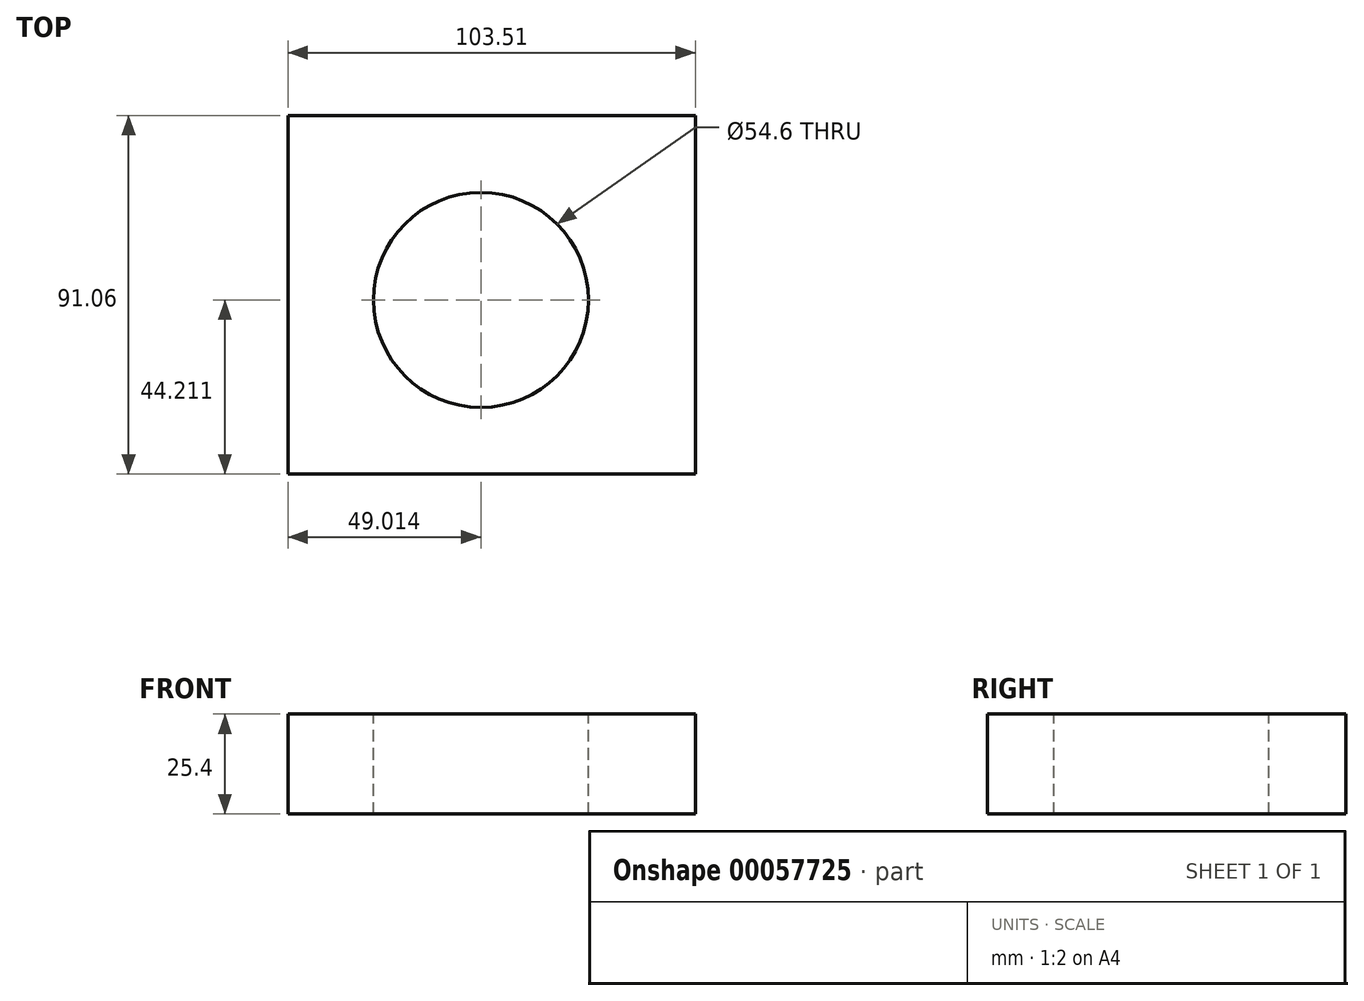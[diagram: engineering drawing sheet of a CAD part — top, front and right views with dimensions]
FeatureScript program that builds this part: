
annotation { "Feature Type Name" : "Feature", "Feature Type Description" : "" }
export const myFeature = defineFeature(function(context is Context, id is Id, definition is map)
    precondition{}
    {
        {
            var Q0;
            Q0=qCreatedBy(makeId("Top.planeOp"),FACE);
            var sketch = newSketch(context, id + "F0", { "sketchPlane" : qUnion([Q0])});
            skLineSegment(sketch, "E0.bottom", {"start": v(-56.32, -38.7) * mm, "end": v(47.2, -38.7) * mm});
            skLineSegment(sketch, "E0.top", {"start": v(-56.32, 52.37) * mm, "end": v(47.2, 52.37) * mm});
            skLineSegment(sketch, "E0.left", {"start": v(-56.32, -38.7) * mm, "end": v(-56.32, 52.37) * mm});
            skLineSegment(sketch, "E0.right", {"start": v(47.2, -38.7) * mm, "end": v(47.2, 52.37) * mm});
            skSolve(sketch);
        }
        {
            var Q0;
            Q0 = qSketchRegion(id + "F0", true);
            extrude(context, id + "F1", {"entities" : qUnion([Q0]), "depth" : 25.4 * mm});
        }
        {
            var Q0;
            Q0=makeQuery(id+"F1.opExtrude","CAP_FACE",FACE,{"disambiguationData":[OSD([sQuery(id+"F0.wireOp",EDGE,"E0.bottom"),sQuery(id+"F0.wireOp",EDGE,"E0.top"),sQuery(id+"F0.wireOp",EDGE,"E0.left"),sQuery(id+"F0.wireOp",EDGE,"E0.right")])],"isStart":false});
            var sketch = newSketch(context, id + "F2", { "sketchPlane" : qUnion([Q0])});
            skCircle(sketch, "E1", {"center": v(-7.3, 5.52) * mm, "radius": 27.3 * mm});
            skSolve(sketch);
        }
        {
            var Q0;
            Q0=makeQuery(id+"F2.imprint","IMPRINT",FACE,{"disambiguationData":[TD([[makeQuery(id+"F2.imprint","IMPRINT",EDGE,{"derivedFrom":sQuery(id+"F2.wireOp",EDGE,"E1")}),1.0]])]});
            extrude(context, id + "F3", {"entities" : qUnion([Q0]), "operationType" : NewBodyOperationType.REMOVE, "endBound" : BoundingType.THROUGH_ALL, "oppositeDirection" : true, "depth" : 25.4 * mm});
        }
    });
